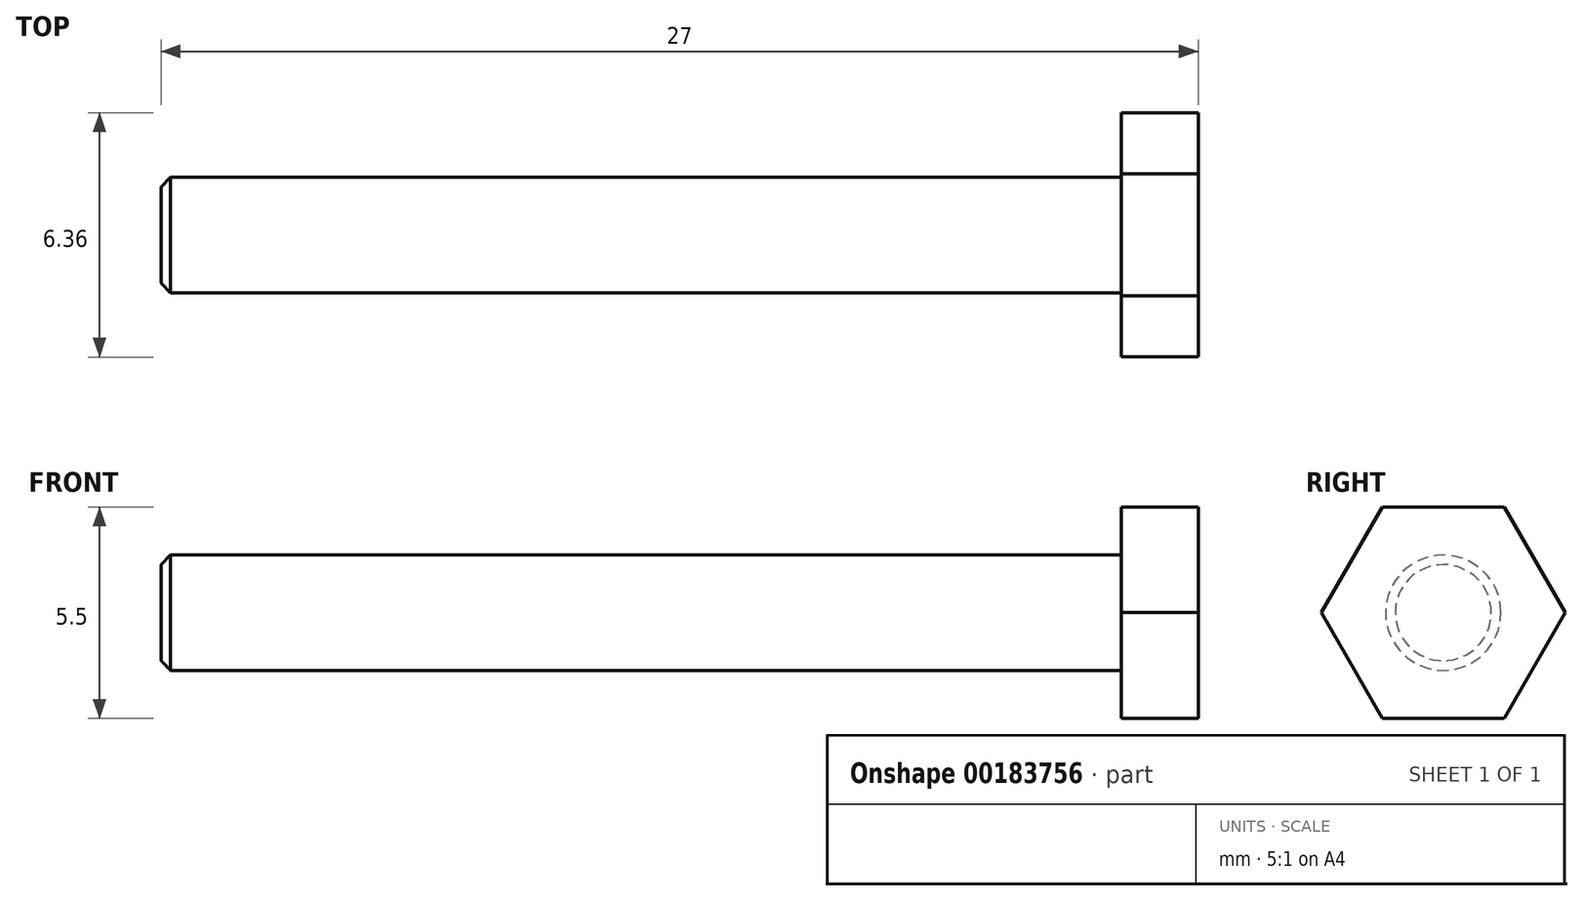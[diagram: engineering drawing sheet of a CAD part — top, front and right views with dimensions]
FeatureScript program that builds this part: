
annotation { "Feature Type Name" : "Feature", "Feature Type Description" : "" }
export const myFeature = defineFeature(function(context is Context, id is Id, definition is map)
    precondition{}
    {
        {
            var Q0;
            Q0=qCreatedBy(makeId("Right.planeOp"),FACE);
            var sketch = newSketch(context, id + "F0", { "sketchPlane" : qUnion([Q0])});
            skCircle(sketch, "E0.cCircle", {"center": v(0, 0) * mm, "radius": 2.75 * mm, "construction": true});
            skLineSegment(sketch, "E0.0", {"start": v(1.59, -2.75) * mm, "end": v(-1.59, -2.75) * mm});
            skLineSegment(sketch, "E0.1", {"start": v(-1.59, -2.75) * mm, "end": v(-3.18, 0) * mm});
            skLineSegment(sketch, "E0.2", {"start": v(-3.18, 0) * mm, "end": v(-1.59, 2.75) * mm});
            skLineSegment(sketch, "E0.3", {"start": v(-1.59, 2.75) * mm, "end": v(1.59, 2.75) * mm});
            skLineSegment(sketch, "E0.4", {"start": v(1.59, 2.75) * mm, "end": v(3.18, 0) * mm});
            skLineSegment(sketch, "E0.5", {"start": v(3.18, 0) * mm, "end": v(1.59, -2.75) * mm});
            skPoint(sketch, "E0.0.midPoint", {"position": v(0, -2.75) * mm});
            skSolve(sketch);
        }
        {
            var Q0;
            Q0 = qSketchRegion(id + "F0", true);
            extrude(context, id + "F1", {"entities" : qUnion([Q0]), "depth" : 2 * mm});
        }
        {
            var Q0;
            Q0=qCreatedBy(makeId("Right.planeOp"),FACE);
            var sketch = newSketch(context, id + "F2", { "sketchPlane" : qUnion([Q0])});
            skCircle(sketch, "E1", {"center": v(0, 0) * mm, "radius": 1.5 * mm});
            skSolve(sketch);
        }
        {
            var Q0;
            Q0=makeQuery(id+"F2.imprint","IMPRINT",FACE,{"disambiguationData":[TD([[makeQuery(id+"F2.imprint","IMPRINT",EDGE,{"derivedFrom":sQuery(id+"F2.wireOp",EDGE,"E1")}),1.0]])]});
            extrude(context, id + "F3", {"entities" : qUnion([Q0]), "operationType" : NewBodyOperationType.ADD, "oppositeDirection" : true, "depth" : 25 * mm});
        }
        {
            var Q0;
            Q0=makeQuery(id+"F3.opExtrude","CAP_EDGE",EDGE,{"disambiguationData":[OSD([sQuery(id+"F2.wireOp",EDGE,"E1")])],"isStart":false});
            chamfer(context, id + "F4", {"entities" : qUnion([Q0]), "width" : .25 * mm, "tangentPropagation" : true});
        }
    });
